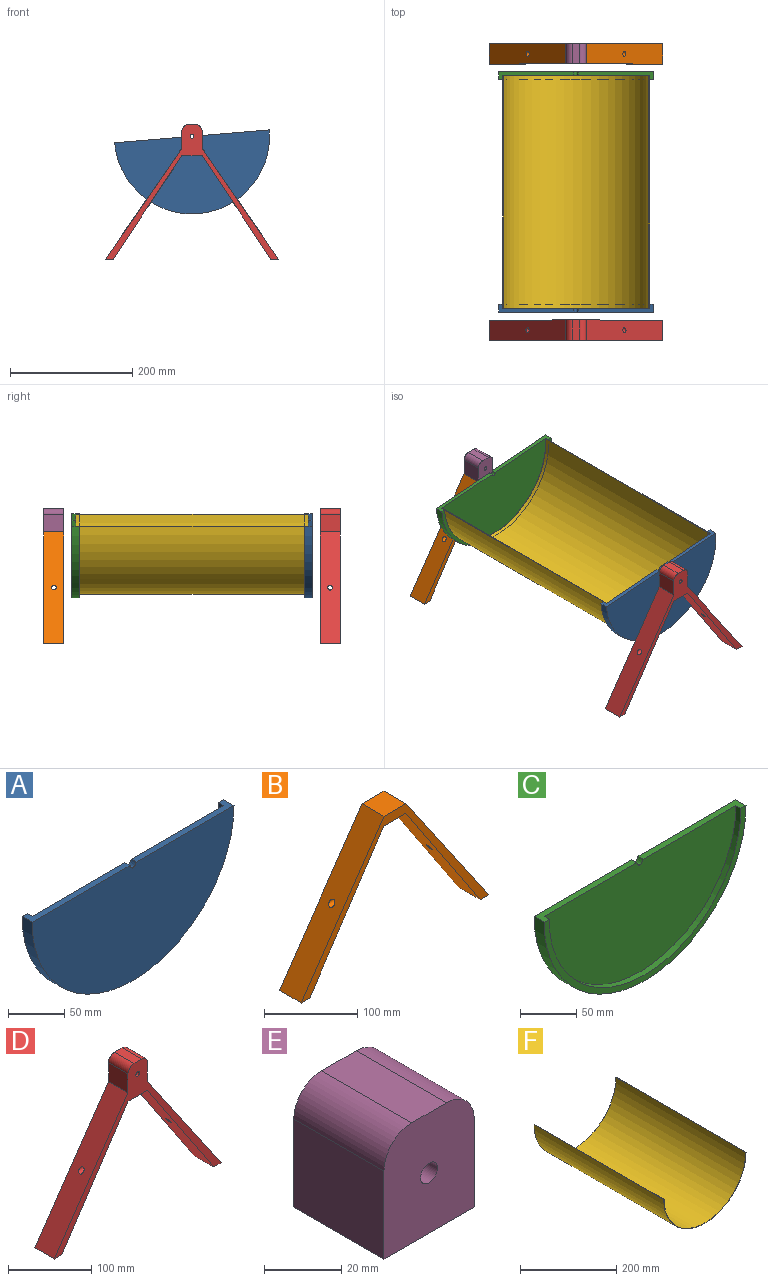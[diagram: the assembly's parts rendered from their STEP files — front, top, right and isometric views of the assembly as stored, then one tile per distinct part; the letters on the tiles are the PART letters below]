
ASSEMBLY  parts=6 mates=5
PART A: 8 faces, bbox 254x12.7x127 mm
  f0: plane 123.19x12.7mm, normal (0,0,1), area 822.6mm2, adj f1,f2,f3,f4,f5,f7
  f1: plane 241.3x120.65mm, normal (0,1,0), area 22842.6mm2, adj f0,f2,f6,f7
  f2: cylinder r=120.65mm len=241.3mm, axis (0,1,0), area 2406.9mm2, adj f0,f1,f3,f6
  f3: plane 254x127mm, normal (0,1,0), area 2470.2mm2, adj f0,f2,f4,f6
  f4: cylinder r=127mm len=254mm, axis (0,1,0), area 5067.1mm2, adj f0,f3,f5,f6
  f5: plane 254x127mm, normal (0,-1,0), area 25312.8mm2, adj f0,f4,f6,f7
  f6: plane 123.19x12.7mm, normal (0,0,1), area 822.6mm2, adj f1,f2,f3,f4,f5,f7
  f7: extruded ~7.62x6.35mm, area 76.9mm2, adj f0,f1,f5,f6
PART B: 12 faces, bbox 283.3x33x182.1 mm
  f0: plane 169.27x112.42mm, normal (-0.83,0,-0.55), area 6654.9mm2, adj f1,f7,f8,f9,f11
  f1: plane 33.02x33.02mm, normal (0,0,-1), area 1090.3mm2, adj f0,f2,f8,f9
  f2: plane 169.27x112.42mm, normal (0.83,0,-0.55), area 6654.9mm2, adj f1,f3,f8,f9,f10
  f3: plane 33.02x12.7mm, normal (0.01,0,-1), area 419.4mm2, adj f2,f4,f8,f9
  f4: plane 182.14x125.12mm, normal (-0.82,0,0.57), area 7241.4mm2, adj f3,f5,f8,f9,f10
  f5: plane 33.02x33.02mm, normal (0,0,1), area 1090.3mm2, adj f4,f6,f8,f9
  f6: plane 182.14x125.12mm, normal (0.82,0,0.57), area 7241.4mm2, adj f5,f7,f8,f9,f11
  f7: plane 33.02x12.7mm, normal (-0.01,0,-1), area 419.4mm2, adj f0,f6,f8,f9
  f8: plane 283.27x182.14mm, normal (0,1,0), area 4138.2mm2, adj f0,f1,f2,f3,f4,f5,f6,f7
  f9: plane 283.27x182.14mm, normal (0,-1,0), area 4138.2mm2, adj f0,f1,f2,f3,f4,f5,f6,f7
  f10: cylinder r=3.81mm len=15.69mm, axis (1,0,0), area 251.6mm2, adj f2,f4
  f11: cylinder r=3.81mm len=15.69mm, axis (-1,0,0), area 251.6mm2, adj f0,f6
PART C: 8 faces, bbox 254x12.7x127 mm
  f0: plane 123.19x12.7mm, normal (0,0,1), area 822.6mm2, adj f1,f2,f3,f4,f5,f7
  f1: plane 241.3x120.65mm, normal (0,-1,0), area 22842.6mm2, adj f0,f2,f6,f7
  f2: cylinder r=120.65mm len=241.3mm, axis (0,-1,0), area 2406.9mm2, adj f0,f1,f3,f6
  f3: plane 254x127mm, normal (0,-1,0), area 2470.2mm2, adj f0,f2,f4,f6
  f4: cylinder r=127mm len=254mm, axis (0,-1,0), area 5067.1mm2, adj f0,f3,f5,f6
  f5: plane 254x127mm, normal (0,1,0), area 25312.8mm2, adj f0,f4,f6,f7
  f6: plane 123.19x12.7mm, normal (0,0,1), area 822.6mm2, adj f1,f2,f3,f4,f5,f7
  f7: extruded ~7.62x6.35mm, area 76.9mm2, adj f0,f1,f5,f6
PART D: 17 faces, bbox 283.3x33x220.2 mm
  f0: plane 169.27x112.42mm, normal (0.83,0,-0.55), area 6654.9mm2, adj f1,f9,f10,f11,f14
  f1: plane 33.02x33.02mm, normal (0,0,-1), area 1090.3mm2, adj f0,f2,f10,f11
  f2: plane 169.27x112.42mm, normal (-0.83,0,-0.55), area 6654.9mm2, adj f1,f3,f10,f11,f15
  f3: plane 33.02x12.7mm, normal (-0.01,0,-1), area 419.4mm2, adj f2,f4,f10,f11
  f4: plane 182.15x125.12mm, normal (0.82,0,0.57), area 7241.4mm2, adj f3,f5,f10,f11,f15
  f5: plane 33.02x27.94mm, normal (1,0,0), area 922.6mm2, adj f4,f10,f11,f12
  f6: plane 33.02x12.7mm, normal (0,0,1), area 419.4mm2, adj f10,f11,f12,f13
  f7: plane 33.02x27.94mm, normal (-1,0,0), area 922.6mm2, adj f8,f10,f11,f13
  f8: plane 182.15x125.12mm, normal (-0.82,0,0.57), area 7241.4mm2, adj f7,f9,f10,f11,f14
  f9: plane 33.02x12.7mm, normal (0.01,0,-1), area 419.4mm2, adj f0,f8,f10,f11
  f10: plane 283.26x220.25mm, normal (0,-1,0), area 5321.2mm2, adj f0,f1,f2,f3,f4,f5,f6,f7
  f11: plane 283.26x220.25mm, normal (0,1,0), area 5321.2mm2, adj f0,f1,f2,f3,f4,f5,f6,f7
  f12: cylinder r=10.16mm len=33.02mm, axis (0,-1,0), area 527mm2, adj f5,f6,f10,f11
  f13: cylinder r=10.16mm len=33.02mm, axis (0,1,0), area 527mm2, adj f6,f7,f10,f11
  f14: cylinder r=3.81mm len=15.7mm, axis (1,0,0), area 251.7mm2, adj f0,f8
  f15: cylinder r=3.81mm len=15.7mm, axis (-1,0,0), area 251.7mm2, adj f2,f4
  f16: cylinder r=3.11mm len=33.02mm, axis (0,1,0), area 645.5mm2, adj f10,f11
PART E: 9 faces, bbox 33x33x38.1 mm
  f0: plane 33.02x27.94mm, normal (1,0,0), area 922.6mm2, adj f1,f5,f6,f8
  f1: plane 33.02x33.02mm, normal (0,0,-1), area 1090.3mm2, adj f0,f2,f5,f6
  f2: plane 33.02x27.94mm, normal (-1,0,0), area 922.6mm2, adj f1,f5,f6,f7
  f3: plane 33.02x12.7mm, normal (0,0,1), area 419.4mm2, adj f5,f6,f7,f8
  f4: cylinder r=3.12mm len=33.02mm, axis (0,-1,0), area 646.7mm2, adj f5,f6
  f5: plane 38.1x33.02mm, normal (0,1,0), area 1183.2mm2, adj f0,f1,f2,f3,f4,f7,f8
  f6: plane 38.1x33.02mm, normal (0,-1,0), area 1183.2mm2, adj f0,f1,f2,f3,f4,f7,f8
  f7: cylinder r=10.16mm len=33.02mm, axis (0,1,0), area 527mm2, adj f2,f3,f5,f6
  f8: cylinder r=10.16mm len=33.02mm, axis (0,-1,0), area 527mm2, adj f0,f3,f5,f6
PART F: 6 faces, bbox 241.3x381x120.7 mm
  f0: plane 381x0.79mm, normal (0,0,1), area 302.4mm2, adj f1,f2,f3,f5
  f1: cylinder r=120.65mm len=381mm, axis (0,1,0), area 144411.6mm2, adj f0,f2,f3,f4
  f2: plane 241.3x120.65mm, normal (0,-1,0), area 299.9mm2, adj f0,f1,f4,f5
  f3: plane 241.3x120.65mm, normal (0,1,0), area 299.9mm2, adj f0,f1,f4,f5
  f4: plane 381x0.79mm, normal (0,0,1), area 302.4mm2, adj f1,f2,f3,f5
  f5: cylinder r=119.86mm len=381mm, axis (0,-1,0), area 143461.6mm2, adj f0,f2,f3,f4
PLACE A rot(axis=(0,-1,0),4.8deg) t=(0,400.05,0)mm
PLACE B t=(0,400.05,0.23)mm
PLACE C rot(axis=(0,-1,0),4.8deg) t=(0,400.05,0)mm
PLACE D t=(0,400.05,0)mm
PLACE E t=(0,400.05,0)mm
PLACE F rot(axis=(0,-1,0),4.8deg) t=(0,400.05,0)mm
MATE fastened A.f2 <-> F.f5  axis (0,1,0) through (0,19.05,0)mm
MATE revolute A.f2 <-> D.f16  axis (0,-1,0) through (0,12.7,0)mm
MATE fastened E.f1 <-> B.f5  axis (0,0,-1) through (0,435.61,-19.05)mm
MATE fastened C.f2 <-> F.f5  axis (0,-1,0) through (0,400.05,0)mm
MATE fastened D.f16 <-> E.f4  axis (0,1,0) through (0,0,0)mm
